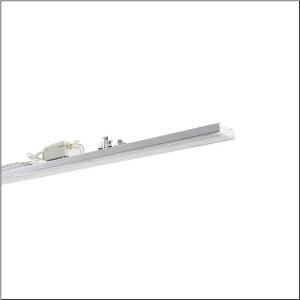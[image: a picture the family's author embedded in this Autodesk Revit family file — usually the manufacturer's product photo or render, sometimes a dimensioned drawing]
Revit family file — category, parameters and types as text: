
# Revit family: licross_21_recessed_ho_52tl12cn4c5m
name_source: partatom
category: Lighting Fixtures
units: mm (PartAtom-declared; Revit-internal decimal feet)

## family parameters
Cut with Voids When Loaded = No
Host = Face
Light Source = No
Part Type = Normal
Room Calculation Point = No
Round Connector Dimension = Use Diameter
Shared = No

## types (1)
- --- (1 x LED, 12670 lm, 68.4 W, 4000K)
    Apparent Load = 68 VA
    CIE Flux Codes = 69 91 98 100 100
    Color Rendering = 80
    Color Temperature = 4000K
    Default Elevation = 1800 mm
    Description = Licross 21 Recessed HO, luminaire insert, of sheet steel, galvanised, coil coated, white, length: 1.500mm, width: 66mm, height: 67mm, LED rated luminous flux: 12.670lm, light colour: 840, SDCM (Standard Deviation of Colour Matching)MacAdam ≤ 3 SDCM (initial), control gear: ON/OFF Multilumen, CLOi, with plug, 3-pole, with phase selection, mains connection: 220..240V, AC, 50/60Hz, start of lifetime: 68W, end of service life: 83W, internal wiring halogen-free, primary optical cover: cover, of PMMA, light emission: direct distribution, primary light characteristic: symmetric, protection rating (complete): IP40, insulation class (complete): insulation class I (protective earthing), certification: CE, ENEC, VDE, UKCA, protection symbol: D if used in an environment without relevant dust loads with corresponding accessories, impact resistance: IK06, permissible ambient temperature for indoor applications: -35..+30°C, corresponds to IFS (International Featured Standards) requirements for safety and quality in the food industry, reducing of maximum allowable ambient temperature of 5°C with ceiling mounting, LABS conformity tested according to VDMA 24364:2018-05, The light source and the operating device comply with the requirements of the Ecodesign Regulation (EU) 2019/2020 and are replaceable in accordance with this regulation, packaging unit: 1 piece
    Height = 58 mm
    Lamp = 1 x LED
    Lamp Light Flux = 12670 lm
    Lamp Power = 68.4 W
    Lamp count = 1
    Length = 1500 mm
    Luminous efficacy = 185 lm/W
    Manufacturer = Siteco
    ModVariant = No
    Model = 52TL12CN4C5M
    Mounting Place = Ceiling
    Mounting Type = Pendant
    Number of Poles = 1
    OnlyDefault = Yes
    Power Factor = 1
    Product Name = Licross 21 Recessed HO
    Product group = luminaire insert | ceiling pendant
    ProductGroupID = 901
    Protection Class = Protection class I
    Protection Degree = IP 40
    RLX_Detail_Level = 1
    RLX_Emergency_Light_Flux = 0 lm
    RLX_Emergency_Type = 0
    RLX_Emergency_Type_DB = No
    RlxData = <blob elided: 22625 chars, md5=194962ce>
    Socket = socket
    Standby Power = 0 W
    System Light Flux = 12670 lm
    System Power = 68 W
    Type Comments = factory setting: luminous flux: 100 % | (A | C | E) | 161 mA
    Type Image = l_1296930.jpg
    URL = http://relux.com
    VarID = @adj_111333
    Voltage = 0 V
    Weight = 0.00 kg
    Width = 66 mm

## geometry (parser evidence)
native form markers: Blend x4, Sweep x10
no freeform markers — native parametric forms only
